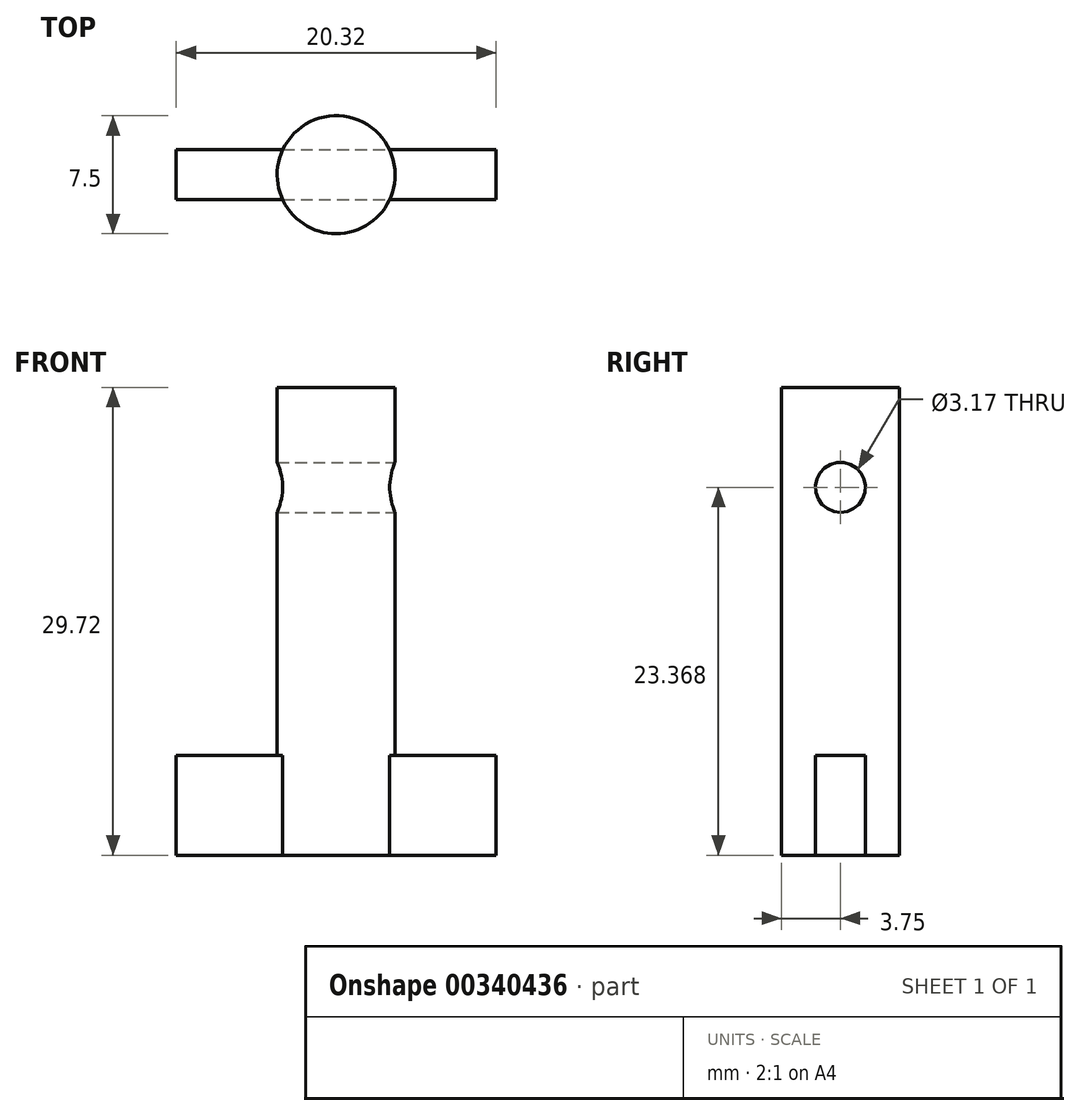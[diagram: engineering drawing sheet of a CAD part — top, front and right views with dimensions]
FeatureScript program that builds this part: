
annotation { "Feature Type Name" : "Feature", "Feature Type Description" : "" }
export const myFeature = defineFeature(function(context is Context, id is Id, definition is map)
    precondition{}
    {
        {
            var Q0;
            Q0=qCreatedBy(makeId("Top.planeOp"),FACE);
            var sketch = newSketch(context, id + "F0", { "sketchPlane" : qUnion([Q0])});
            skCircle(sketch, "E0", {"center": v(0, 0) * mm, "radius": 3.75 * mm});
            skSolve(sketch);
        }
        {
            var Q0;
            Q0=makeQuery(id+"F0.imprint","IMPRINT",FACE,{"disambiguationData":[TD([[makeQuery(id+"F0.imprint","IMPRINT",EDGE,{"derivedFrom":sQuery(id+"F0.wireOp",EDGE,"E0")}),1.0]])]});
            extrude(context, id + "F1", {"entities" : qUnion([Q0]), "depth" : 29.72 * mm});
        }
        {
            var Q0;
            Q0=qCreatedBy(makeId("Right.planeOp"),FACE);
            var sketch = newSketch(context, id + "F2", { "sketchPlane" : qUnion([Q0])});
            skLineSegment(sketch, "E1", {"start": v(0, 0) * mm, "end": v(-1.59, 0) * mm});
            skLineSegment(sketch, "E2", {"start": v(-1.59, 0) * mm, "end": v(-1.59, 6.35) * mm});
            skLineSegment(sketch, "E3", {"start": v(-1.59, 6.35) * mm, "end": v(0, 6.35) * mm});
            skLineSegment(sketch, "E4", {"start": v(0, 6.35) * mm, "end": v(0, 0) * mm});
            skLineSegment(sketch, "E5.MirrorCS", {"start": v(1.59, 6.35) * mm, "end": v(0, 6.35) * mm});
            skLineSegment(sketch, "E6.MirrorCS", {"start": v(1.59, 0) * mm, "end": v(1.59, 6.35) * mm});
            skLineSegment(sketch, "E7.MirrorCS", {"start": v(0, 0) * mm, "end": v(1.59, 0) * mm});
            skSolve(sketch);
        }
        {
            var Q0;
            Q0 = qSketchRegion(id + "F2", true);
            extrude(context, id + "F3", {"entities" : qUnion([Q0]), "operationType" : NewBodyOperationType.ADD, "endBound" : BoundingType.SYMMETRIC, "depth" : 20.32 * mm});
        }
        {
            var Q0;
            Q0=makeQuery(id+"F3.opExtrude","CAP_FACE",FACE,{"disambiguationData":[OSD([sQuery(id+"F2.wireOp",EDGE,"E1"),sQuery(id+"F2.wireOp",EDGE,"E2"),sQuery(id+"F2.wireOp",EDGE,"E3"),sQuery(id+"F2.wireOp",EDGE,"E5.MirrorCS"),sQuery(id+"F2.wireOp",EDGE,"E6.MirrorCS"),sQuery(id+"F2.wireOp",EDGE,"E7.MirrorCS")])],"isStart":false});
            var sketch = newSketch(context, id + "F4", { "sketchPlane" : qUnion([Q0])});
            skCircle(sketch, "E8", {"center": v(0, 23.37) * mm, "radius": 1.59 * mm});
            skSolve(sketch);
        }
        {
            var Q0;
            Q0=makeQuery(id+"F4.imprint","IMPRINT",FACE,{"disambiguationData":[TD([[makeQuery(id+"F4.imprint","IMPRINT",EDGE,{"derivedFrom":sQuery(id+"F4.wireOp",EDGE,"E8")}),1.0]])]});
            extrude(context, id + "F5", {"entities" : qUnion([Q0]), "operationType" : NewBodyOperationType.REMOVE, "oppositeDirection" : true, "depth" : 25.4 * mm});
        }
    });
